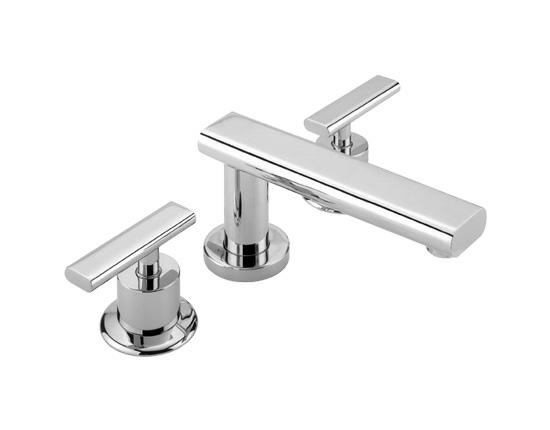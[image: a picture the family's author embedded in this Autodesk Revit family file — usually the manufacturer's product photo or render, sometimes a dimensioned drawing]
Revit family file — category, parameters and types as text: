
# Revit family: Mezcladora de Lavabo MEP-2115
name_source: partatom
category: Plumbing Fixtures
revit_build: Autodesk Revit 2015 (Build: 20140223_1515(x64)
units: mm (PartAtom-declared; Revit-internal decimal feet)

## types (1)
- MEP-2115
    Brass Chromed = Brass
    Default Elevation = 1"
    Description = Ensamble de 8" a 12" con desagüe de push.
    Features = Incluye herramienta de sujeción, contra de desagüe automático con rebosadero y aireador.
    Inlet Threads = ½" - 14 NPSM
    Installation Adjustment = Instalación a  8", 10" y 12"
    Manufacturer = HELVEX S.A. de C.V.
    Max. Working Pressure = 85.3 psi
    Min. Working Pressure = 2.9 psi
    Model = MEP-2115
    Satin = Satín
    Support Base Diameter = 2"
    Total Height = 4"
    Total Length = 12"
    Total Width = 6"
    Type Comments = Mezcladora de 8" a 12"
    Type Image = MEP-2115.jpg
    URL = http://www.helvex.com.mx

## geometry (parser evidence)
native form markers: Sweep x3
no freeform markers — native parametric forms only
